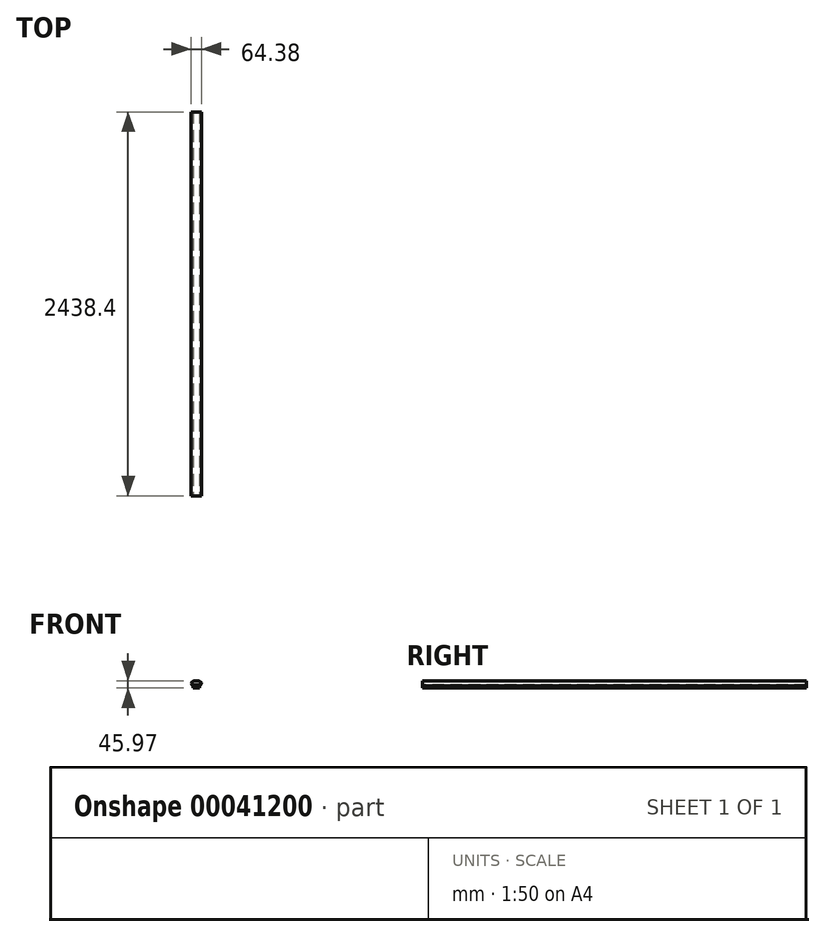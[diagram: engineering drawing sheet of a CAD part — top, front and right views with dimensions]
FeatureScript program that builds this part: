
annotation { "Feature Type Name" : "Feature", "Feature Type Description" : "" }
export const myFeature = defineFeature(function(context is Context, id is Id, definition is map)
    precondition{}
    {
        {
            var Q0;
            Q0=qCreatedBy(makeId("Front.planeOp"),FACE);
            var sketch = newSketch(context, id + "F0", { "sketchPlane" : qUnion([Q0])});
            skLineSegment(sketch, "E0", {"start": v(-21.46, 0) * mm, "end": v(21.46, 0) * mm});
            skLineSegment(sketch, "E1", {"start": v(21.46, 0) * mm, "end": v(21.46, -5.18) * mm});
            skLineSegment(sketch, "E2", {"start": v(21.46, -5.18) * mm, "end": v(24.63, -5.18) * mm});
            skLineSegment(sketch, "E3", {"start": v(24.63, -5.18) * mm, "end": v(24.63, -4.3) * mm});
            skLineSegment(sketch, "E4", {"start": v(-21.46, 0) * mm, "end": v(-21.46, -5.18) * mm});
            skLineSegment(sketch, "E5", {"start": v(-21.46, -5.18) * mm, "end": v(-24.63, -5.18) * mm});
            skLineSegment(sketch, "E6", {"start": v(-24.63, -5.18) * mm, "end": v(-24.63, -4.3) * mm});
            skLineSegment(sketch, "E7", {"start": v(0, 0) * mm, "end": v(0, 26.92) * mm, "construction": true});
            skLineSegment(sketch, "E8", {"start": v(0, 9.53) * mm, "end": v(32.2, 9.53) * mm, "construction": true});
            skPoint(sketch, "E9.newPointB", {"position": v(-24.63, 0) * mm});
            skPoint(sketch, "E10.orphan", {"position": v(24.63, 0) * mm});
            skEllipticalArc(sketch, "E11", {});
            skArc(sketch, "E12.filletArc", {"start": v(-24.63, -4.3) * mm, "mid": v(-25.14, -2.08) * mm, "end": v(-26.56, -0.3) * mm});
            skArc(sketch, "E13.filletArc", {"start": v(26.56, -0.3) * mm, "mid": v(25.14, -2.08) * mm, "end": v(24.63, -4.3) * mm});
            skPoint(sketch, "E14", {"position": v(32.2, 9.53) * mm});
            skPoint(sketch, "E15", {"position": v(-32.2, 9.53) * mm});
            const initialGuessF0  = {"E11": [0, 0.009525, 1, 0, 0.03219450000000001, 0.017399, 5.682801300798814, 3.7419766599705655]};
            skSetInitialGuess(sketch, initialGuessF0);
            skSolve(sketch);
        }
        {
            var Q0;
            Q0 = qSketchRegion(id + "F0", true);
            extrude(context, id + "F1", {"entities" : qUnion([Q0]), "oppositeDirection" : true, "depth" : 2438.4 * mm});
        }
        {
            var Q0;
            Q0=qCreatedBy(makeId("Front.planeOp"),FACE);
            var sketch = newSketch(context, id + "F2", { "sketchPlane" : qUnion([Q0])});
            skLineSegment(sketch, "E16.bottom", {"start": v(-21.46, 0) * mm, "end": v(21.46, 0) * mm});
            skLineSegment(sketch, "E16.top", {"start": v(-21.46, -19.05) * mm, "end": v(21.46, -19.05) * mm});
            skLineSegment(sketch, "E16.left", {"start": v(-21.46, 0) * mm, "end": v(-21.46, -19.05) * mm});
            skLineSegment(sketch, "E16.right", {"start": v(21.46, 0) * mm, "end": v(21.46, -19.05) * mm});
            skSolve(sketch);
        }
        {
            var Q0;
            Q0=makeQuery(id+"F2.imprint","IMPRINT",FACE,{"disambiguationData":[TD([[makeQuery(id+"F2.imprint","IMPRINT",EDGE,{"derivedFrom":sQuery(id+"F2.wireOp",EDGE,"E16.bottom")}),-1.0]])]});
            extrude(context, id + "F3", {"entities" : qUnion([Q0]), "oppositeDirection" : true, "depth" : 2438.4 * mm});
        }
        {
            var Q0;
            Q0=makeQuery(id+"F3.opExtrude","SWEPT_FACE",FACE,{"disambiguationData":[OSD([sQuery(id+"F2.wireOp",EDGE,"E16.top")])]});
            var sketch = newSketch(context, id + "F4", { "sketchPlane" : qUnion([Q0])});
            skLineSegment(sketch, "E17", {"start": v(0, 0) * mm, "end": v(0, -2438.4) * mm});
            skPoint(sketch, "E18", {"position": v(0, -101.6) * mm});
            skSolve(sketch);
        }
        {
            var Q0;
            Q0=makeQuery(id+"F1.opExtrude","SWEPT_FACE",FACE,{"disambiguationData":[OSD([sQuery(id+"F0.wireOp",EDGE,"E0")])]});
            var sketch = newSketch(context, id + "F5", { "sketchPlane" : qUnion([Q0])});
            skLineSegment(sketch, "E19", {"start": v(0, 0) * mm, "end": v(0, -150.28) * mm});
            skPoint(sketch, "E20", {"position": v(0, -101.6) * mm});
            skSolve(sketch);
        }
        {
            var Q0;
            Q0=makeQuery(id+"F1.opExtrude","CAP_FACE",FACE,{"disambiguationData":[OSD([sQuery(id+"F0.wireOp",EDGE,"E0"),sQuery(id+"F0.wireOp",EDGE,"E1"),sQuery(id+"F0.wireOp",EDGE,"E2"),sQuery(id+"F0.wireOp",EDGE,"E3"),sQuery(id+"F0.wireOp",EDGE,"E4"),sQuery(id+"F0.wireOp",EDGE,"E5"),sQuery(id+"F0.wireOp",EDGE,"E6"),sQuery(id+"F0.wireOp",EDGE,"E11"),sQuery(id+"F0.wireOp",EDGE,"E12.filletArc"),sQuery(id+"F0.wireOp",EDGE,"E13.filletArc")])],"isStart":false});
            var sketch = newSketch(context, id + "F6", { "sketchPlane" : qUnion([Q0])});
            skLineSegment(sketch, "E21", {"start": v(0, 0) * mm, "end": v(0, 26.92) * mm});
            skSolve(sketch);
        }
    });
